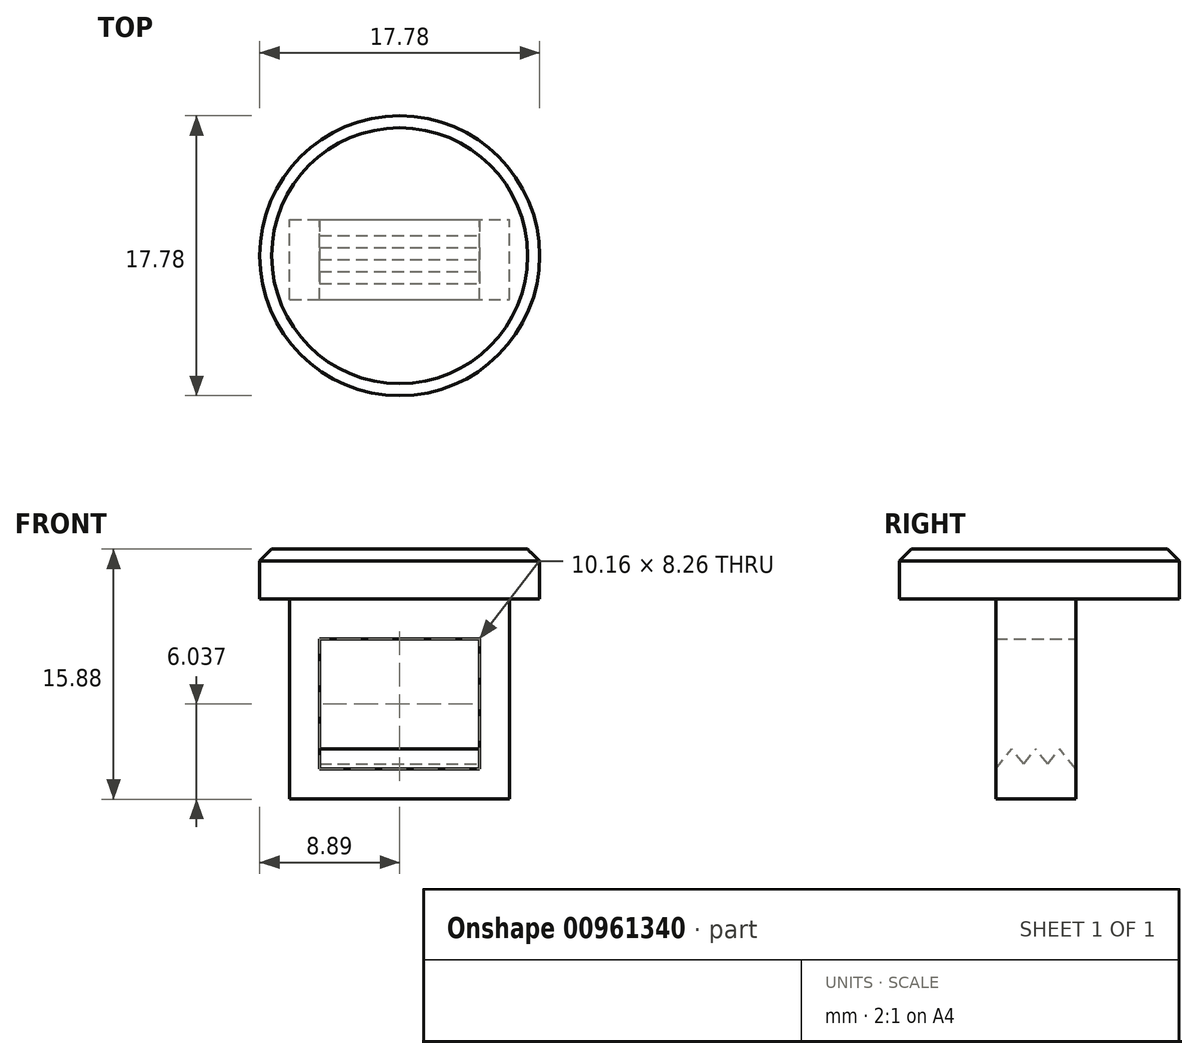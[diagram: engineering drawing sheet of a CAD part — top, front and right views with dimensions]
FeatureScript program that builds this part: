
annotation { "Feature Type Name" : "Feature", "Feature Type Description" : "" }
export const myFeature = defineFeature(function(context is Context, id is Id, definition is map)
    precondition{}
    {
        {
            var Q0;
            Q0=qCreatedBy(makeId("Front.planeOp"),FACE);
            var sketch = newSketch(context, id + "F0", { "sketchPlane" : qUnion([Q0])});
            skLineSegment(sketch, "E0.bottom", {"start": v(-6.99, 3.18) * mm, "end": v(6.98, 3.18) * mm});
            skLineSegment(sketch, "E0.top", {"start": v(-6.99, -9.53) * mm, "end": v(6.99, -9.53) * mm});
            skLineSegment(sketch, "E0.left", {"start": v(-6.99, 3.18) * mm, "end": v(-6.99, -9.53) * mm});
            skLineSegment(sketch, "E0.right", {"start": v(6.99, 3.18) * mm, "end": v(6.99, -9.53) * mm});
            skLineSegment(sketch, "E1.bottom", {"start": v(-5.08, -7.62) * mm, "end": v(5.08, -7.62) * mm});
            skLineSegment(sketch, "E1.top", {"start": v(-5.08, 0.64) * mm, "end": v(5.08, 0.64) * mm});
            skLineSegment(sketch, "E1.left", {"start": v(-5.08, -7.62) * mm, "end": v(-5.08, 0.64) * mm});
            skLineSegment(sketch, "E1.right", {"start": v(5.08, -7.62) * mm, "end": v(5.08, 0.64) * mm});
            skSolve(sketch);
        }
        {
            var Q0;
            Q0=makeQuery(id+"F0.imprint","IMPRINT",FACE,{"disambiguationData":[TD([[makeQuery(id+"F0.imprint","IMPRINT",EDGE,{"derivedFrom":sQuery(id+"F0.wireOp",EDGE,"E0.bottom")}),-1.0]])]});
            extrude(context, id + "F1", {"entities" : qUnion([Q0]), "depth" : 5.08 * mm, "offsetDistance" : 25.4 * mm});
        }
        {
            var Q0;
            Q0=makeQuery(id+"F1.opExtrude","SWEPT_FACE",FACE,{"disambiguationData":[OSD([sQuery(id+"F0.wireOp",EDGE,"E0.bottom")])]});
            var sketch = newSketch(context, id + "F2", { "sketchPlane" : qUnion([Q0])});
            skCircle(sketch, "E2", {"center": v(0, -2.3) * mm, "radius": 8.9 * mm});
            skSolve(sketch);
        }
        {
            var Q0;
            Q0 = qSketchRegion(id + "F2", true);
            extrude(context, id + "F3", {"entities" : qUnion([Q0]), "operationType" : NewBodyOperationType.ADD, "depth" : 3.17 * mm, "offsetDistance" : 25.4 * mm});
        }
        {
            var Q0;
            Q0=makeQuery(id+"F3.opExtrude","CAP_EDGE",EDGE,{"disambiguationData":[OSD([sQuery(id+"F2.wireOp",EDGE,"E2")])],"isStart":false});
            chamfer(context, id + "F4", {"entities" : qUnion([Q0]), "width" : 0.76 * mm, "tangentPropagation" : true});
        }
        {
            var Q0;
            Q0=makeQuery(id+"F1.opExtrude","SWEPT_FACE",FACE,{"disambiguationData":[OSD([sQuery(id+"F0.wireOp",EDGE,"E1.right")])]});
            var sketch = newSketch(context, id + "F5", { "sketchPlane" : qUnion([Q0])});
            skLineSegment(sketch, "E3.MirrorCS", {"start": v(5.08, -7.62) * mm, "end": v(4.06, -6.35) * mm});
            skLineSegment(sketch, "E4.MirrorCS", {"start": v(3.3, -7.3) * mm, "end": v(4.06, -6.35) * mm});
            skLineSegment(sketch, "E5.MirrorCS", {"start": v(3.3, -7.3) * mm, "end": v(2.54, -6.35) * mm});
            skLineSegment(sketch, "E6.MirrorCS", {"start": v(1.78, -7.3) * mm, "end": v(2.54, -6.35) * mm});
            skLineSegment(sketch, "E7.MirrorCS", {"start": v(1.78, -7.3) * mm, "end": v(1.02, -6.35) * mm});
            skLineSegment(sketch, "E8.MirrorCS", {"start": v(0, -7.62) * mm, "end": v(1.02, -6.35) * mm});
            skSolve(sketch);
        }
        {
            var Q0;
            Q0=makeQuery(id+"F5.imprint","IMPRINT",FACE,{"disambiguationData":[TD([[makeQuery(id+"F5.imprint","IMPRINT",EDGE,{"derivedFrom":sQuery(id+"F5.wireOp",EDGE,"E3.MirrorCS")}),1.0]])]});
            extrude(context, id + "F6", {"entities" : qUnion([Q0]), "operationType" : NewBodyOperationType.ADD, "depth" : 10.16 * mm, "offsetDistance" : 25.4 * mm});
        }
    });
